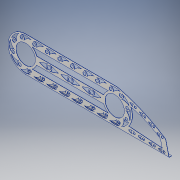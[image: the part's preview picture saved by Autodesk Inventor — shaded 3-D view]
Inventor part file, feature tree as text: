
AUTODESK INVENTOR PART (.ipt)
format: ipt  version: 2016 (Build 200138000, 138)  size: 539,136 bytes
history: native  units: in
note: dims shown in document units (in); Inventor stores cm internally (conversion verified against a paired STEP export)
features: reference x9, sheet_metal_op x7, other x3, sketch x2
ambient origin geometry x8: Origin, YZ Plane, XZ Plane, XY Plane, X Axis, Y Axis, Z Axis, Center Point
bodies: Solid1 (feature_tree)
feature tree (21):
  sheet_metal_op  "Face1"
  sheet_metal_op  "Flange1"
  sheet_metal_op  "Flange2"
  reference  "Reference3"
  reference  "Reference4"
  reference  "Reference5"
  reference  "Reference6"
  reference  "Reference7"
  reference  "Reference8"
  reference  "Reference9"
  reference  "Reference10"
  reference  "Reference11"
  other  "Plate1"
  sketch  "Sketch2"  dims[d1=0.2in]
  other  "Plate2"
  sheet_metal_op  "Bend1"
  sheet_metal_op  "Corner1"
  sketch  "Sketch3"  dims[d2=0.2in d10=0.8in d16=1.9685in d17=0.8in d36=5.0in d37=5.0in d42=1.0in d43=1.0in d44=3.0in d45=6.0in d46=1.0in d47=1.5in d48=0.7874in d50=5.5in d51=0.7874in d53=5.5in d57=1.9685in d59=0.7874in d61=0.7874in d62=1.9685in d64=180.0deg d66=1.9685in d68=180.0deg d70=2.7559in d72=3.25in d73=0.3937in d75=1.0in d77=2.7559in d79=3.25in d80=0.3937in d82=1.0in d87=3.2675in d89=0.6in d90=0.444in d92=0.7874in d94=0.7874in d96=1.9685in d98=1.9685in d100=2.7559in d102=0.3937in d104=2.7559in d106=0.3937in d110=0.7874in d112=0.7874in d114=1.9685in d116=1.9685in d118=2.7559in d120=0.3937in d122=2.7559in d124=0.3937in d128=0.7874in d130=0.7874in d132=1.9685in d134=1.9685in d136=2.7559in d138=0.3937in d140=2.7559in d142=0.3937in d146=0.7874in d148=0.7874in d150=1.9685in d152=1.9685in d154=2.7559in d156=0.3937in d158=2.7559in d160=0.3937in d164=0.7874in d166=0.7874in d168=1.9685in d170=1.9685in d172=2.7559in d174=0.3937in d176=2.7559in d178=0.3937in d182=0.7874in d184=0.7874in d186=1.9685in d188=1.9685in d190=2.7559in d192=0.3937in d194=2.7559in d196=0.3937in d200=0.7874in d202=0.7874in d204=1.9685in d206=1.9685in d208=2.7559in d210=0.3937in d212=2.7559in d214=0.3937in d218=0.7874in d220=0.7874in d222=1.9685in d224=1.9685in d226=2.7559in d228=0.3937in d230=2.7559in d232=0.3937in d233=0.6in d234=0.444in d236=0.7874in d238=0.7874in d240=1.9685in d242=1.9685in d244=2.7559in d246=0.3937in d248=2.7559in d250=0.3937in d251=0.6in d252=0.444in d254=0.7874in d256=0.7874in d258=1.9685in d260=1.9685in d262=2.7559in d264=0.3937in d266=2.7559in d268=0.3937in d269=0.6in d270=0.444in d272=0.7874in d274=0.7874in d276=1.9685in d278=1.9685in d280=2.7559in d282=0.3937in d284=2.7559in d286=0.3937in d287=0.6in d288=0.444in d290=0.7874in d292=0.7874in d294=1.9685in d296=1.9685in d298=2.7559in d300=0.3937in d302=2.7559in d304=0.3937in d305=0.6in d306=0.444in d308=0.7874in d310=0.7874in d312=1.9685in d314=1.9685in d316=2.7559in d318=0.3937in d320=2.7559in d322=0.3937in d323=0.6in d324=0.444in d326=0.7874in d328=0.7874in d330=1.9685in d332=1.9685in d334=2.7559in d336=0.3937in d338=2.7559in d340=0.3937in d341=0.6in d342=0.444in d344=0.7874in d346=0.7874in d348=1.9685in d350=1.9685in d352=2.7559in d354=0.3937in d356=2.7559in d358=0.3937in d360=0.064in d361=0.064in d362=0.032in d363=0.128in d364=0.064in d365=0.75in d366=90.0deg d367=0.064in d368=0.256in d369=0.064in d370=0.064in d371=0.064in d372=0.032in d373=0.128in d374=0.064in d375=0.75in d376=90.0deg d377=0.064in d378=0.256in d379=0.064in d380=0.064in]
  other  "Plate3"
  sheet_metal_op  "Bend2"
  sheet_metal_op  "Corner2"
